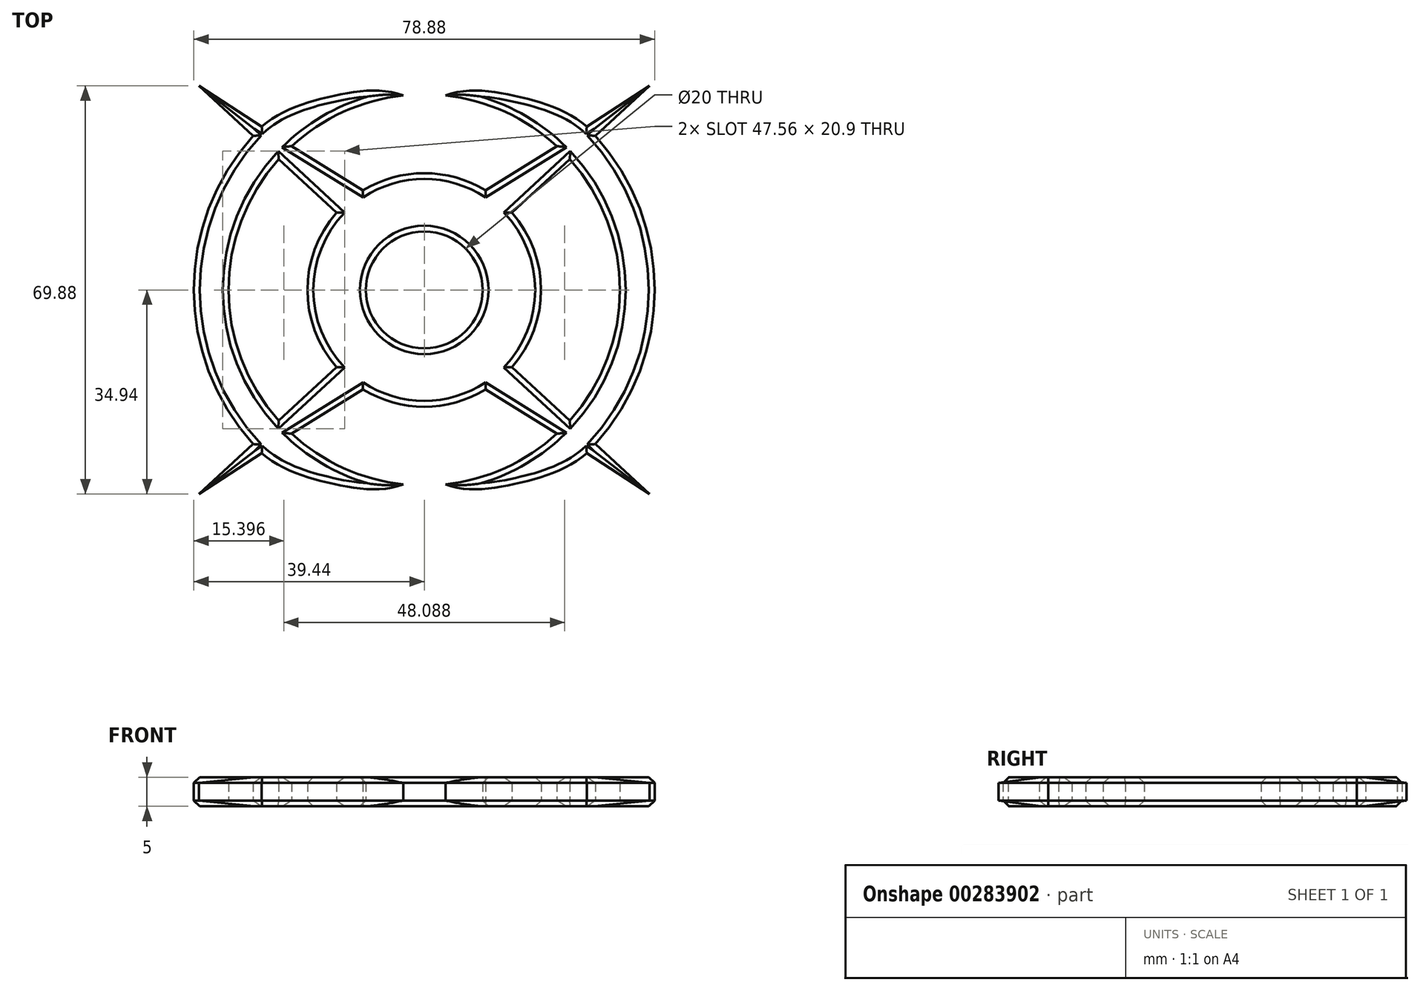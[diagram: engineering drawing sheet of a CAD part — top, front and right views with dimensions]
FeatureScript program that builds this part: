
annotation { "Feature Type Name" : "Feature", "Feature Type Description" : "" }
export const myFeature = defineFeature(function(context is Context, id is Id, definition is map)
    precondition{}
    {
        {
            var Q0;
            Q0=qCreatedBy(makeId("Top.planeOp"),FACE);
            var sketch = newSketch(context, id + "F0", { "sketchPlane" : qUnion([Q0])});
            skArc(sketch, "E0", {"start": v(0, 10) * mm, "mid": v(-7.07, 7.07) * mm, "end": v(-10, 0) * mm});
            skArc(sketch, "E1", {"start": v(0, 20) * mm, "mid": v(-14.14, 14.14) * mm, "end": v(-20, 0) * mm});
            skLineSegment(sketch, "E2", {"start": v(-15, 13.22) * mm, "end": v(-24.93, 22.37) * mm});
            skLineSegment(sketch, "E3", {"start": v(-24.93, 22.37) * mm, "end": v(-38.55, 34.94) * mm});
            skLineSegment(sketch, "E4", {"start": v(-38.55, 34.94) * mm, "end": v(-22.71, 24.62) * mm});
            skLineSegment(sketch, "E5", {"start": v(-22.71, 24.62) * mm, "end": v(-10.48, 17.03) * mm});
            skLineSegment(sketch, "E6", {"start": v(0, 10) * mm, "end": v(0, 20) * mm});
            skLineSegment(sketch, "E7", {"start": v(-10, 0) * mm, "end": v(-20, 0) * mm});
            skArc(sketch, "E8", {"start": v(-3.62, 33.3) * mm, "mid": v(-24.93, 22.37) * mm, "end": v(-33.5, 0) * mm});
            skArc(sketch, "E9", {"start": v(-27.82, 27.95) * mm, "mid": v(-36.42, 15.13) * mm, "end": v(-39.44, 0) * mm});
            skFitSpline(sketch, "E10", {"points": [v(-27.82, 27.95) * mm, v(-15.7, 33.2) * mm, v(-3.62, 33.3) * mm], "startDerivative": vector(18.78, 16.77) * mm, "endDerivative": vector(22.67, -8.58) * mm});
            skLineSegment(sketch, "E11.trimOffspring", {"start": v(-33.5, 0) * mm, "end": v(-39.44, 0) * mm});
            skSolve(sketch);
        }
        {
            var Q0;
            Q0 = qSketchRegion(id + "F0", true);
            extrude(context, id + "F1", {"entities" : qUnion([Q0]), "depth" : 2.5 * mm});
        }
        {
            var Q0;
            {var subQ0=sQuery(id+"F0.wireOp",EDGE,"E8");Q0=makeQuery(id+"F1.opExtrude","CAP_EDGE",EDGE,{"disambiguationData":[OSD([subQ0]),TDD([makeQuery(id+"F0.imprint","IMPRINT",EDGE,{"disambiguationData":[TD([[makeQuery(id+"F0.imprint","INTERSECT",VERTEX,{"derivedFrom":[subQ0,sQuery(id+"F0.wireOp",EDGE,"E11.trimOffspring")]}),1.0]])],"derivedFrom":subQ0})])],"isStart":false});}
            var Q1;
            Q1=makeQuery(id+"F1.opExtrude","CAP_EDGE",EDGE,{"disambiguationData":[OSD([sQuery(id+"F0.wireOp",EDGE,"E2")])],"isStart":false});
            var Q2;
            Q2=makeQuery(id+"F1.opExtrude","CAP_EDGE",EDGE,{"disambiguationData":[OSD([sQuery(id+"F0.wireOp",EDGE,"E5")])],"isStart":false});
            var Q3;
            {var subQ0=sQuery(id+"F0.wireOp",EDGE,"E8");Q3=makeQuery(id+"F1.opExtrude","CAP_EDGE",EDGE,{"disambiguationData":[OSD([subQ0]),TDD([makeQuery(id+"F0.imprint","IMPRINT",EDGE,{"disambiguationData":[TD([[makeQuery(id+"F0.imprint","INTERSECT",VERTEX,{"derivedFrom":[subQ0,sQuery(id+"F0.wireOp",EDGE,"E10")]}),-1.0]])],"derivedFrom":subQ0})])],"isStart":false});}
            var Q4;
            Q4=makeQuery(id+"F1.opExtrude","CAP_EDGE",EDGE,{"disambiguationData":[OSD([sQuery(id+"F0.wireOp",EDGE,"E3")])],"isStart":false});
            var Q5;
            Q5=makeQuery(id+"F1.opExtrude","CAP_EDGE",EDGE,{"disambiguationData":[OSD([sQuery(id+"F0.wireOp",EDGE,"E4")])],"isStart":false});
            var Q6;
            Q6=makeQuery(id+"F1.opExtrude","CAP_EDGE",EDGE,{"disambiguationData":[OSD([sQuery(id+"F0.wireOp",EDGE,"E10")])],"isStart":false});
            var Q7;
            Q7=makeQuery(id+"F1.opExtrude","CAP_EDGE",EDGE,{"disambiguationData":[OSD([sQuery(id+"F0.wireOp",EDGE,"E9")])],"isStart":false});
            var Q8;
            Q8=makeQuery(id+"F1.opExtrude","CAP_EDGE",EDGE,{"disambiguationData":[OSD([sQuery(id+"F0.wireOp",EDGE,"E0")])],"isStart":false});
            var Q9;
            {var subQ0=sQuery(id+"F0.wireOp",EDGE,"E1");Q9=makeQuery(id+"F1.opExtrude","CAP_EDGE",EDGE,{"disambiguationData":[OSD([subQ0]),TDD([makeQuery(id+"F0.imprint","IMPRINT",EDGE,{"disambiguationData":[TD([[makeQuery(id+"F0.imprint","INTERSECT",VERTEX,{"derivedFrom":[subQ0,sQuery(id+"F0.wireOp",EDGE,"E7")]}),1.0]])],"derivedFrom":subQ0})])],"isStart":false});}
            var Q10;
            {var subQ0=sQuery(id+"F0.wireOp",EDGE,"E1");Q10=makeQuery(id+"F1.opExtrude","CAP_EDGE",EDGE,{"disambiguationData":[OSD([subQ0]),TDD([makeQuery(id+"F0.imprint","IMPRINT",EDGE,{"disambiguationData":[TD([[makeQuery(id+"F0.imprint","INTERSECT",VERTEX,{"derivedFrom":[subQ0,sQuery(id+"F0.wireOp",EDGE,"E6")]}),-1.0]])],"derivedFrom":subQ0})])],"isStart":false});}
            chamfer(context, id + "F2", {"entities" : qUnion([Q0, Q1, Q2, Q3, Q4, Q5, Q6, Q7, Q8, Q9, Q10]), "width" : 1 * mm, "tangentPropagation" : true});
        }
        {
            var Q0;
            Q0=makeQuery(id+"F1.opExtrude","SWEPT_BODY",BODY,{"disambiguationData":[OSD([sQuery(id+"F0.wireOp",EDGE,"E0"),sQuery(id+"F0.wireOp",EDGE,"E1"),sQuery(id+"F0.wireOp",EDGE,"E2"),sQuery(id+"F0.wireOp",EDGE,"E3"),sQuery(id+"F0.wireOp",EDGE,"E4"),sQuery(id+"F0.wireOp",EDGE,"E5"),sQuery(id+"F0.wireOp",EDGE,"E8"),sQuery(id+"F0.wireOp",EDGE,"E9"),sQuery(id+"F0.wireOp",EDGE,"E10"),sQuery(id+"F0.wireOp",EDGE,"E6"),sQuery(id+"F0.wireOp",EDGE,"E7"),sQuery(id+"F0.wireOp",EDGE,"E11.trimOffspring")])]});
            var Q1;
            Q1=qCreatedBy(makeId("Top.planeOp"),FACE);
            mirror(context, id + "F3", {"operationType" : NewBodyOperationType.ADD, "entities" : qUnion([Q0]), "mirrorPlane" : qUnion([Q1])});
        }
        {
            var Q0;
            Q0=makeQuery(id+"F1.opExtrude","SWEPT_BODY",BODY,{"disambiguationData":[OSD([sQuery(id+"F0.wireOp",EDGE,"E0"),sQuery(id+"F0.wireOp",EDGE,"E1"),sQuery(id+"F0.wireOp",EDGE,"E2"),sQuery(id+"F0.wireOp",EDGE,"E3"),sQuery(id+"F0.wireOp",EDGE,"E4"),sQuery(id+"F0.wireOp",EDGE,"E5"),sQuery(id+"F0.wireOp",EDGE,"E8"),sQuery(id+"F0.wireOp",EDGE,"E9"),sQuery(id+"F0.wireOp",EDGE,"E10"),sQuery(id+"F0.wireOp",EDGE,"E6"),sQuery(id+"F0.wireOp",EDGE,"E7"),sQuery(id+"F0.wireOp",EDGE,"E11.trimOffspring")])]});
            var Q1;
            Q1=qCreatedBy(makeId("Front.planeOp"),FACE);
            mirror(context, id + "F4", {"operationType" : NewBodyOperationType.ADD, "entities" : qUnion([Q0]), "mirrorPlane" : qUnion([Q1])});
        }
        {
            var Q0;
            Q0=makeQuery(id+"F1.opExtrude","SWEPT_BODY",BODY,{"disambiguationData":[OSD([sQuery(id+"F0.wireOp",EDGE,"E0"),sQuery(id+"F0.wireOp",EDGE,"E1"),sQuery(id+"F0.wireOp",EDGE,"E2"),sQuery(id+"F0.wireOp",EDGE,"E3"),sQuery(id+"F0.wireOp",EDGE,"E4"),sQuery(id+"F0.wireOp",EDGE,"E5"),sQuery(id+"F0.wireOp",EDGE,"E8"),sQuery(id+"F0.wireOp",EDGE,"E9"),sQuery(id+"F0.wireOp",EDGE,"E10"),sQuery(id+"F0.wireOp",EDGE,"E6"),sQuery(id+"F0.wireOp",EDGE,"E7"),sQuery(id+"F0.wireOp",EDGE,"E11.trimOffspring")])]});
            var Q1;
            Q1=qCreatedBy(makeId("Right.planeOp"),FACE);
            mirror(context, id + "F5", {"operationType" : NewBodyOperationType.ADD, "entities" : qUnion([Q0]), "mirrorPlane" : qUnion([Q1])});
        }
    });
